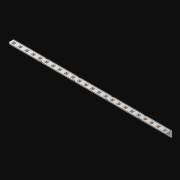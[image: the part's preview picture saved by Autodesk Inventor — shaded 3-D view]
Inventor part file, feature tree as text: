
AUTODESK INVENTOR PART (.ipt)
format: ipt  version: 2021 (Build 250183000, 183)  size: 758,784 bytes
history: native  units: in
note: dims shown in document units (in); Inventor stores cm internally (conversion verified against a paired STEP export)
features: extrude x49, other x48, sketch x3, pattern_linear x1, sheet_metal_op x1
ambient origin geometry x8: Origin, YZ Plane, XZ Plane, XY Plane, X Axis, Y Axis, Z Axis, Center Point
bodies: Solid1 (feature_tree)
feature tree (102):
  pattern_linear  "Rectangular Pattern1"  Spacing1=0.063in  [1 undecoded]
  extrude  "Extrusion1"  Depth=0.5in
  sketch  "Sketch1"  dims[d0=0.182in]
  other  "Srf1"
  sketch  "Sketch2"  dims[d1=0.063in d2=0.0in]
  other  "Srf2"
  other  "Srf3"
  other  "Srf5"
  other  "Srf7"
  other  "Srf9"
  other  "Srf11"
  other  "Srf13"
  other  "Srf15"
  other  "Srf17"
  other  "Srf19"
  other  "Srf21"
  other  "Srf23"
  other  "Srf25"
  other  "Srf27"
  other  "Srf29"
  other  "Srf31"
  other  "Srf33"
  other  "Srf35"
  other  "Srf37"
  other  "Srf39"
  other  "Srf41"
  other  "Srf43"
  other  "Srf45"
  other  "Srf47"
  other  "Srf4"
  other  "Srf6"
  other  "Srf8"
  other  "Srf10"
  other  "Srf12"
  other  "Srf14"
  other  "Srf16"
  other  "Srf18"
  other  "Srf20"
  other  "Srf22"
  other  "Srf24"
  other  "Srf26"
  other  "Srf28"
  other  "Srf30"
  other  "Srf32"
  other  "Srf34"
  other  "Srf36"
  other  "Srf38"
  other  "Srf40"
  other  "Srf42"
  other  "Srf44"
  other  "Srf46"
  other  "Srf48"
  sketch  "Sketch3"  dims[d3=0.182in d4=0.063in d5=0.0in d8=0.5in d9=5.5in d10=0.0in]
  sheet_metal_op  "Fold1"
  extrude  "ExtrusionSrf1"  Depth=5.5in TaperAngle=0.0deg
  extrude  "ExtrusionSrf2"  [1 undecoded]
  extrude  "ExtrusionSrf3"  [1 undecoded]
  extrude  "ExtrusionSrf4"  [1 undecoded]
  extrude  "ExtrusionSrf5"  [1 undecoded]
  extrude  "ExtrusionSrf6"  [1 undecoded]
  extrude  "ExtrusionSrf7"  [1 undecoded]
  extrude  "ExtrusionSrf8"  [1 undecoded]
  extrude  "ExtrusionSrf9"  [1 undecoded]
  extrude  "ExtrusionSrf10"  [1 undecoded]
  extrude  "ExtrusionSrf11"  [1 undecoded]
  extrude  "ExtrusionSrf12"  [1 undecoded]
  extrude  "ExtrusionSrf13"  [1 undecoded]
  extrude  "ExtrusionSrf14"  [1 undecoded]
  extrude  "ExtrusionSrf15"  [1 undecoded]
  extrude  "ExtrusionSrf16"  [1 undecoded]
  extrude  "ExtrusionSrf17"  [1 undecoded]
  extrude  "ExtrusionSrf18"  [1 undecoded]
  extrude  "ExtrusionSrf19"  [1 undecoded]
  extrude  "ExtrusionSrf20"  [1 undecoded]
  extrude  "ExtrusionSrf21"  [1 undecoded]
  extrude  "ExtrusionSrf22"  [1 undecoded]
  extrude  "ExtrusionSrf23"  [1 undecoded]
  extrude  "ExtrusionSrf24"  [1 undecoded]
  extrude  "ExtrusionSrf25"  [1 undecoded]
  extrude  "ExtrusionSrf37"  [1 undecoded]
  extrude  "ExtrusionSrf38"  [1 undecoded]
  extrude  "ExtrusionSrf39"  [1 undecoded]
  extrude  "ExtrusionSrf40"  [1 undecoded]
  extrude  "ExtrusionSrf41"  [1 undecoded]
  extrude  "ExtrusionSrf42"  [1 undecoded]
  extrude  "ExtrusionSrf43"  [1 undecoded]
  extrude  "ExtrusionSrf44"  [1 undecoded]
  extrude  "ExtrusionSrf45"  [1 undecoded]
  extrude  "ExtrusionSrf46"  [1 undecoded]
  extrude  "ExtrusionSrf47"  [1 undecoded]
  extrude  "ExtrusionSrf48"  [1 undecoded]
  extrude  "ExtrusionSrf49"  [1 undecoded]
  extrude  "ExtrusionSrf50"  [1 undecoded]
  extrude  "ExtrusionSrf51"  [1 undecoded]
  extrude  "ExtrusionSrf52"  [1 undecoded]
  extrude  "ExtrusionSrf53"  [1 undecoded]
  extrude  "ExtrusionSrf54"  [1 undecoded]
  extrude  "ExtrusionSrf55"  [1 undecoded]
  extrude  "ExtrusionSrf56"  [1 undecoded]
  extrude  "ExtrusionSrf57"  [1 undecoded]
  extrude  "ExtrusionSrf58"  [1 undecoded]
  extrude  "ExtrusionSrf59"  [1 undecoded]
note: 48 required parameter values undecoded (feature->parameter linkage not recoverable at this tier; creation-order binding heuristic only, values carry confidence <= 0.55)
